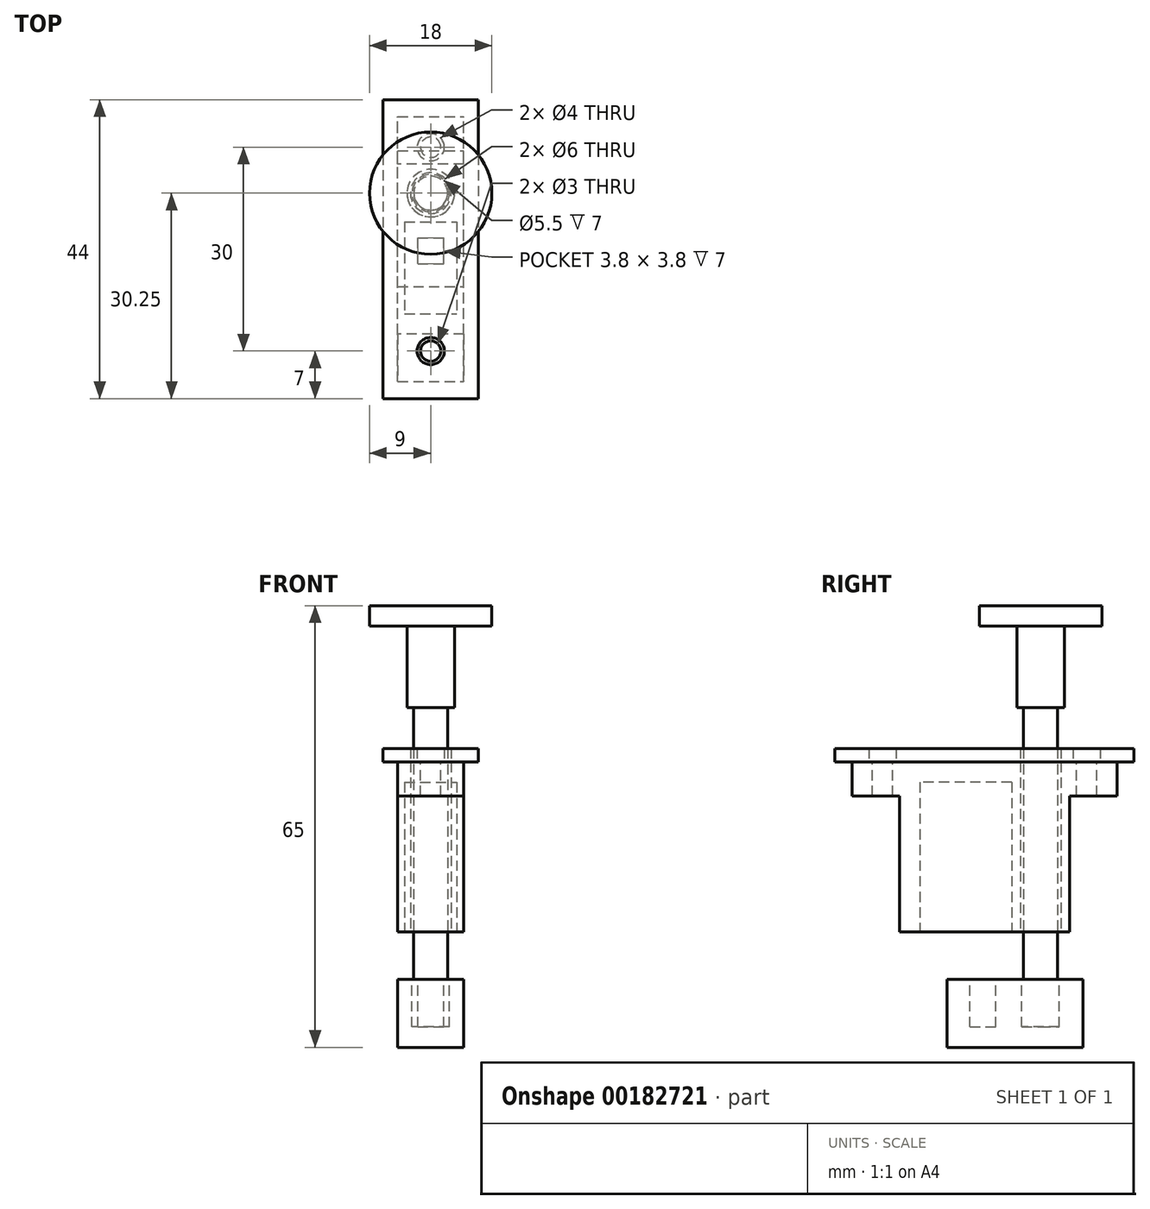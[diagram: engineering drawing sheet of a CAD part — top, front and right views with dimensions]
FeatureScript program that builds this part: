
annotation { "Feature Type Name" : "Feature", "Feature Type Description" : "" }
export const myFeature = defineFeature(function(context is Context, id is Id, definition is map)
    precondition{}
    {
        {
            var Q0;
            Q0=qCreatedBy(makeId("Top.planeOp"),FACE);
            var sketch = newSketch(context, id + "F0", { "sketchPlane" : qUnion([Q0])});
            skLineSegment(sketch, "E0.bottom", {"start": v(4.85, -12.5) * mm, "end": v(-4.85, -12.5) * mm});
            skLineSegment(sketch, "E0.top", {"start": v(4.85, 12.5) * mm, "end": v(-4.85, 12.5) * mm});
            skLineSegment(sketch, "E0.left", {"start": v(4.85, -12.5) * mm, "end": v(4.85, 12.5) * mm});
            skLineSegment(sketch, "E0.right", {"start": v(-4.85, -12.5) * mm, "end": v(-4.85, 12.5) * mm});
            skPoint(sketch, "E0.middle", {"position": v(0, 0) * mm});
            skLineSegment(sketch, "E1.bottom", {"start": v(-3.85, 4) * mm, "end": v(3.85, 4) * mm});
            skLineSegment(sketch, "E1.top", {"start": v(-3.85, -9.5) * mm, "end": v(3.85, -9.5) * mm});
            skLineSegment(sketch, "E1.left", {"start": v(-3.85, 4) * mm, "end": v(-3.85, -9.5) * mm});
            skLineSegment(sketch, "E1.right", {"start": v(3.85, 4) * mm, "end": v(3.85, -9.5) * mm});
            skCircle(sketch, "E2", {"center": v(0, 8.25) * mm, "radius": 3 * mm});
            skSolve(sketch);
        }
        {
            var Q0;
            Q0 = qSketchRegion(id + "F0", true);
            extrude(context, id + "F1", {"entities" : qUnion([Q0]), "depth" : 25 * mm});
        }
        {
            var Q0;
            Q0=makeQuery(id+"F1.opExtrude","CAP_FACE",FACE,{"disambiguationData":[OSD([sQuery(id+"F0.wireOp",EDGE,"E0.bottom"),sQuery(id+"F0.wireOp",EDGE,"E0.top"),sQuery(id+"F0.wireOp",EDGE,"E0.left"),sQuery(id+"F0.wireOp",EDGE,"E0.right"),sQuery(id+"F0.wireOp",EDGE,"E1.bottom"),sQuery(id+"F0.wireOp",EDGE,"E1.top"),sQuery(id+"F0.wireOp",EDGE,"E1.left"),sQuery(id+"F0.wireOp",EDGE,"E1.right"),sQuery(id+"F0.wireOp",EDGE,"E2")])],"isStart":false});
            var sketch = newSketch(context, id + "F2", { "sketchPlane" : qUnion([Q0])});
            skLineSegment(sketch, "E3.bottom", {"start": v(-3.85, 4) * mm, "end": v(3.85, 4) * mm});
            skLineSegment(sketch, "E3.top", {"start": v(-3.85, -9.5) * mm, "end": v(3.85, -9.5) * mm});
            skLineSegment(sketch, "E3.left", {"start": v(-3.85, 4) * mm, "end": v(-3.85, -9.5) * mm});
            skLineSegment(sketch, "E3.right", {"start": v(3.85, 4) * mm, "end": v(3.85, -9.5) * mm});
            skSolve(sketch);
        }
        {
            var Q0;
            Q0 = qSketchRegion(id + "F2", true);
            extrude(context, id + "F3", {"entities" : qUnion([Q0]), "operationType" : NewBodyOperationType.ADD, "oppositeDirection" : true, "depth" : 3 * mm});
        }
        {
            var Q0;
            Q0=makeQuery(id+"F3.boolean.opBoolean","MERGE",FACE,{"derivedFrom":[makeQuery(id+"F1.opExtrude","CAP_FACE",FACE,{"disambiguationData":[OSD([sQuery(id+"F0.wireOp",EDGE,"E0.bottom"),sQuery(id+"F0.wireOp",EDGE,"E0.top"),sQuery(id+"F0.wireOp",EDGE,"E0.left"),sQuery(id+"F0.wireOp",EDGE,"E0.right"),sQuery(id+"F0.wireOp",EDGE,"E1.bottom"),sQuery(id+"F0.wireOp",EDGE,"E1.top"),sQuery(id+"F0.wireOp",EDGE,"E1.left"),sQuery(id+"F0.wireOp",EDGE,"E1.right"),sQuery(id+"F0.wireOp",EDGE,"E2")])],"isStart":false}),makeQuery(id+"F3.opExtrude","CAP_FACE",FACE,{"disambiguationData":[OSD([sQuery(id+"F2.wireOp",EDGE,"E3.bottom"),sQuery(id+"F2.wireOp",EDGE,"E3.top"),sQuery(id+"F2.wireOp",EDGE,"E3.left"),sQuery(id+"F2.wireOp",EDGE,"E3.right")])],"isStart":true})]});
            var sketch = newSketch(context, id + "F4", { "sketchPlane" : qUnion([Q0])});
            skLineSegment(sketch, "E4.bottom", {"start": v(-4.85, 12.5) * mm, "end": v(4.85, 12.5) * mm});
            skLineSegment(sketch, "E4.top", {"start": v(-4.85, 19.5) * mm, "end": v(4.85, 19.5) * mm});
            skLineSegment(sketch, "E4.left", {"start": v(-4.85, 12.5) * mm, "end": v(-4.85, 19.5) * mm});
            skLineSegment(sketch, "E4.right", {"start": v(4.85, 12.5) * mm, "end": v(4.85, 19.5) * mm});
            skLineSegment(sketch, "E5.bottom", {"start": v(-4.85, -12.5) * mm, "end": v(4.85, -12.5) * mm});
            skLineSegment(sketch, "E5.top", {"start": v(-4.85, -19.5) * mm, "end": v(4.85, -19.5) * mm});
            skLineSegment(sketch, "E5.left", {"start": v(-4.85, -12.5) * mm, "end": v(-4.85, -19.5) * mm});
            skLineSegment(sketch, "E5.right", {"start": v(4.85, -12.5) * mm, "end": v(4.85, -19.5) * mm});
            skCircle(sketch, "E6", {"center": v(0, 15) * mm, "radius": 1.5 * mm});
            skCircle(sketch, "E7", {"center": v(0, -15) * mm, "radius": 1.5 * mm});
            skPoint(sketch, "E7.centerSnap0", {"position": v(0, 12.5) * mm});
            skSolve(sketch);
        }
        {
            var Q0;
            Q0 = qSketchRegion(id + "F4", true);
            extrude(context, id + "F5", {"entities" : qUnion([Q0]), "operationType" : NewBodyOperationType.ADD, "oppositeDirection" : true, "depth" : 5 * mm});
        }
        {
            var Q0;
            Q0=makeQuery(id+"F5.boolean.opBoolean","MERGE",FACE,{"derivedFrom":[makeQuery(id+"F3.boolean.opBoolean","MERGE",FACE,{"derivedFrom":[makeQuery(id+"F1.opExtrude","CAP_FACE",FACE,{"disambiguationData":[OSD([sQuery(id+"F0.wireOp",EDGE,"E0.bottom"),sQuery(id+"F0.wireOp",EDGE,"E0.top"),sQuery(id+"F0.wireOp",EDGE,"E0.left"),sQuery(id+"F0.wireOp",EDGE,"E0.right"),sQuery(id+"F0.wireOp",EDGE,"E1.bottom"),sQuery(id+"F0.wireOp",EDGE,"E1.top"),sQuery(id+"F0.wireOp",EDGE,"E1.left"),sQuery(id+"F0.wireOp",EDGE,"E1.right"),sQuery(id+"F0.wireOp",EDGE,"E2")])],"isStart":false}),makeQuery(id+"F3.opExtrude","CAP_FACE",FACE,{"disambiguationData":[OSD([sQuery(id+"F2.wireOp",EDGE,"E3.bottom"),sQuery(id+"F2.wireOp",EDGE,"E3.top"),sQuery(id+"F2.wireOp",EDGE,"E3.left"),sQuery(id+"F2.wireOp",EDGE,"E3.right")])],"isStart":true})]}),makeQuery(id+"F5.opExtrude","CAP_FACE",FACE,{"disambiguationData":[OSD([sQuery(id+"F4.wireOp",EDGE,"E4.bottom"),sQuery(id+"F4.wireOp",EDGE,"E4.top"),sQuery(id+"F4.wireOp",EDGE,"E4.left"),sQuery(id+"F4.wireOp",EDGE,"E4.right"),sQuery(id+"F4.wireOp",EDGE,"E6")])],"isStart":true}),makeQuery(id+"F5.opExtrude","CAP_FACE",FACE,{"disambiguationData":[OSD([sQuery(id+"F4.wireOp",EDGE,"E5.bottom"),sQuery(id+"F4.wireOp",EDGE,"E5.top"),sQuery(id+"F4.wireOp",EDGE,"E5.left"),sQuery(id+"F4.wireOp",EDGE,"E5.right"),sQuery(id+"F4.wireOp",EDGE,"E7")])],"isStart":true})]});
            var sketch = newSketch(context, id + "F6", { "sketchPlane" : qUnion([Q0])});
            skCircle(sketch, "E8", {"center": v(0, 8.25) * mm, "radius": 2.5 * mm});
            skSolve(sketch);
        }
        {
            var Q0;
            Q0 = qSketchRegion(id + "F6", true);
            extrude(context, id + "F7", {"entities" : qUnion([Q0]), "depth" : 20 * mm, "hasSecondDirection" : true, "secondDirectionOppositeDirection" : true, "secondDirectionDepth" : 32 * mm});
        }
        {
            var Q0;
            Q0=makeQuery(id+"F7.opExtrude","CAP_FACE",FACE,{"disambiguationData":[OSD([sQuery(id+"F6.wireOp",EDGE,"E8")])],"isStart":true});
            var sketch = newSketch(context, id + "F8", { "sketchPlane" : qUnion([Q0])});
            skLineSegment(sketch, "E9.bottom", {"start": v(-4.85, 5.5) * mm, "end": v(4.85, 5.5) * mm});
            skLineSegment(sketch, "E9.top", {"start": v(-4.85, -14.5) * mm, "end": v(4.85, -14.5) * mm});
            skLineSegment(sketch, "E9.left", {"start": v(-4.85, 5.5) * mm, "end": v(-4.85, -14.5) * mm});
            skLineSegment(sketch, "E9.right", {"start": v(4.85, 5.5) * mm, "end": v(4.85, -14.5) * mm});
            skSolve(sketch);
        }
        {
            var Q0;
            Q0 = qSketchRegion(id + "F8", true);
            extrude(context, id + "F9", {"entities" : qUnion([Q0]), "depth" : 10 * mm});
        }
        {
            var Q0;
            Q0=makeQuery(id+"F9.opExtrude","CAP_FACE",FACE,{"disambiguationData":[OSD([sQuery(id+"F8.wireOp",EDGE,"E9.bottom"),sQuery(id+"F8.wireOp",EDGE,"E9.top"),sQuery(id+"F8.wireOp",EDGE,"E9.left"),sQuery(id+"F8.wireOp",EDGE,"E9.right")])],"isStart":true});
            var sketch = newSketch(context, id + "F10", { "sketchPlane" : qUnion([Q0])});
            skCircle(sketch, "E10", {"center": v(0, 8.25) * mm, "radius": 2.75 * mm});
            skLineSegment(sketch, "E11.bottom", {"start": v(-1.9, -2.15) * mm, "end": v(1.9, -2.15) * mm});
            skLineSegment(sketch, "E11.top", {"start": v(-1.9, 1.65) * mm, "end": v(1.9, 1.65) * mm});
            skLineSegment(sketch, "E11.left", {"start": v(-1.9, -2.15) * mm, "end": v(-1.9, 1.65) * mm});
            skLineSegment(sketch, "E11.right", {"start": v(1.9, -2.15) * mm, "end": v(1.9, 1.65) * mm});
            skPoint(sketch, "E11.middle", {"position": v(0, -0.25) * mm});
            skSolve(sketch);
        }
        {
            var Q0;
            Q0 = qSketchRegion(id + "F10", true);
            extrude(context, id + "F11", {"entities" : qUnion([Q0]), "operationType" : NewBodyOperationType.REMOVE, "oppositeDirection" : true, "depth" : 7 * mm});
        }
        {
            var Q0;
            Q0=makeQuery(id+"F7.opExtrude","CAP_FACE",FACE,{"disambiguationData":[OSD([sQuery(id+"F6.wireOp",EDGE,"E8")])],"isStart":false});
            var sketch = newSketch(context, id + "F12", { "sketchPlane" : qUnion([Q0])});
            skCircle(sketch, "E12", {"center": v(0, 8.25) * mm, "radius": 9 * mm});
            skSolve(sketch);
        }
        {
            var Q0;
            Q0 = qSketchRegion(id + "F12", true);
            extrude(context, id + "F13", {"entities" : qUnion([Q0]), "operationType" : NewBodyOperationType.ADD, "depth" : 3 * mm});
        }
        {
            var Q0;
            Q0=makeQuery(id+"F5.boolean.opBoolean","MERGE",FACE,{"derivedFrom":[makeQuery(id+"F3.boolean.opBoolean","MERGE",FACE,{"derivedFrom":[makeQuery(id+"F1.opExtrude","CAP_FACE",FACE,{"disambiguationData":[OSD([sQuery(id+"F0.wireOp",EDGE,"E0.bottom"),sQuery(id+"F0.wireOp",EDGE,"E0.top"),sQuery(id+"F0.wireOp",EDGE,"E0.left"),sQuery(id+"F0.wireOp",EDGE,"E0.right"),sQuery(id+"F0.wireOp",EDGE,"E1.bottom"),sQuery(id+"F0.wireOp",EDGE,"E1.top"),sQuery(id+"F0.wireOp",EDGE,"E1.left"),sQuery(id+"F0.wireOp",EDGE,"E1.right"),sQuery(id+"F0.wireOp",EDGE,"E2")])],"isStart":false}),makeQuery(id+"F3.opExtrude","CAP_FACE",FACE,{"disambiguationData":[OSD([sQuery(id+"F2.wireOp",EDGE,"E3.bottom"),sQuery(id+"F2.wireOp",EDGE,"E3.top"),sQuery(id+"F2.wireOp",EDGE,"E3.left"),sQuery(id+"F2.wireOp",EDGE,"E3.right")])],"isStart":true})]}),makeQuery(id+"F5.opExtrude","CAP_FACE",FACE,{"disambiguationData":[OSD([sQuery(id+"F4.wireOp",EDGE,"E4.bottom"),sQuery(id+"F4.wireOp",EDGE,"E4.top"),sQuery(id+"F4.wireOp",EDGE,"E4.left"),sQuery(id+"F4.wireOp",EDGE,"E4.right"),sQuery(id+"F4.wireOp",EDGE,"E6")])],"isStart":true}),makeQuery(id+"F5.opExtrude","CAP_FACE",FACE,{"disambiguationData":[OSD([sQuery(id+"F4.wireOp",EDGE,"E5.bottom"),sQuery(id+"F4.wireOp",EDGE,"E5.top"),sQuery(id+"F4.wireOp",EDGE,"E5.left"),sQuery(id+"F4.wireOp",EDGE,"E5.right"),sQuery(id+"F4.wireOp",EDGE,"E7")])],"isStart":true})]});
            var sketch = newSketch(context, id + "F14", { "sketchPlane" : qUnion([Q0])});
            skLineSegment(sketch, "E13.bottom", {"start": v(7, 22) * mm, "end": v(-7, 22) * mm});
            skLineSegment(sketch, "E13.top", {"start": v(7, -22) * mm, "end": v(-7, -22) * mm});
            skLineSegment(sketch, "E13.left", {"start": v(7, 22) * mm, "end": v(7, -22) * mm});
            skLineSegment(sketch, "E13.right", {"start": v(-7, 22) * mm, "end": v(-7, -22) * mm});
            skPoint(sketch, "E13.middle", {"position": v(0, 0) * mm});
            skCircle(sketch, "E14", {"center": v(0, 15) * mm, "radius": 2 * mm});
            skCircle(sketch, "E15", {"center": v(0, -15) * mm, "radius": 2 * mm});
            skCircle(sketch, "E16", {"center": v(0, 8.25) * mm, "radius": 3 * mm});
            skSolve(sketch);
        }
        {
            var Q0;
            Q0 = qSketchRegion(id + "F14", true);
            extrude(context, id + "F15", {"entities" : qUnion([Q0]), "depth" : 2 * mm});
        }
        {
            var Q0;
            Q0=makeQuery(id+"F13.opExtrude","CAP_FACE",FACE,{"disambiguationData":[OSD([sQuery(id+"F12.wireOp",EDGE,"E12")])],"isStart":true});
            var sketch = newSketch(context, id + "F16", { "sketchPlane" : qUnion([Q0])});
            skCircle(sketch, "E17", {"center": v(0, -8.25) * mm, "radius": 3.5 * mm});
            skSolve(sketch);
        }
        {
            var Q0;
            Q0 = qSketchRegion(id + "F16", true);
            extrude(context, id + "F17", {"entities" : qUnion([Q0]), "operationType" : NewBodyOperationType.ADD, "depth" : 12 * mm});
        }
    });
